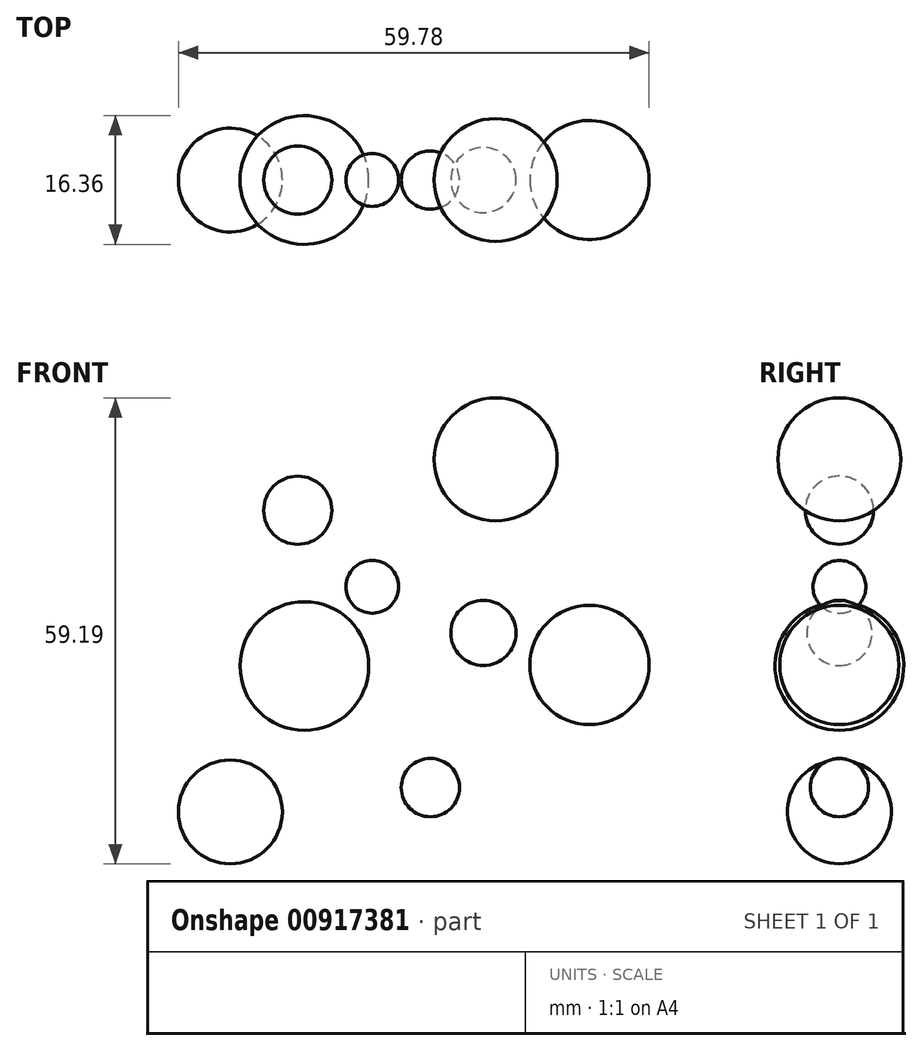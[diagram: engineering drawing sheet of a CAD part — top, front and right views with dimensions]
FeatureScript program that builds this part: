
annotation { "Feature Type Name" : "Feature", "Feature Type Description" : "" }
export const myFeature = defineFeature(function(context is Context, id is Id, definition is map)
    precondition{}
    {
        {
            var Q0;
            Q0=qCreatedBy(makeId("Front.planeOp"),FACE);
            var sketch = newSketch(context, id + "F0", { "sketchPlane" : qUnion([Q0])});
            skCircle(sketch, "E0", {"center": v(0, 0) * mm, "radius": 3.35 * mm});
            skCircle(sketch, "E1", {"center": v(15.65, 16.19) * mm, "radius": 7.81 * mm});
            skCircle(sketch, "E2", {"center": v(-9.47, 9.73) * mm, "radius": 4.34 * mm});
            skCircle(sketch, "E3", {"center": v(-8.63, -10.06) * mm, "radius": 8.18 * mm});
            skCircle(sketch, "E4", {"center": v(27.59, -9.92) * mm, "radius": 7.57 * mm});
            skCircle(sketch, "E5", {"center": v(14.1, -5.85) * mm, "radius": 4.15 * mm});
            skCircle(sketch, "E6", {"center": v(7.37, -25.5) * mm, "radius": 3.7 * mm});
            skCircle(sketch, "E7", {"center": v(-18.03, -28.6) * mm, "radius": 6.6 * mm});
            skPoint(sketch, "E8", {"position": v(-8.63, -1.89) * mm});
            skPoint(sketch, "E9", {"position": v(-8.63, -18.24) * mm});
            skPoint(sketch, "E10", {"position": v(-18.03, -22) * mm});
            skPoint(sketch, "E11", {"position": v(-18.03, -35.19) * mm});
            skPoint(sketch, "E12", {"position": v(7.37, -21.8) * mm});
            skPoint(sketch, "E13", {"position": v(7.37, -29.2) * mm});
            skPoint(sketch, "E14", {"position": v(27.59, -17.49) * mm});
            skPoint(sketch, "E15", {"position": v(27.59, -2.36) * mm});
            skPoint(sketch, "E16", {"position": v(14.1, -10) * mm});
            skPoint(sketch, "E17", {"position": v(14.1, -1.7) * mm});
            skPoint(sketch, "E18", {"position": v(0, 3.35) * mm});
            skPoint(sketch, "E19", {"position": v(0, -3.35) * mm});
            skPoint(sketch, "E20", {"position": v(-9.47, 14.07) * mm});
            skPoint(sketch, "E21", {"position": v(-9.47, 5.4) * mm});
            skPoint(sketch, "E22", {"position": v(15.65, 8.37) * mm});
            skPoint(sketch, "E23", {"position": v(15.65, 24) * mm});
            skLineSegment(sketch, "E24", {"start": v(-9.47, 14.07) * mm, "end": v(-9.47, 5.4) * mm});
            skLineSegment(sketch, "E25", {"start": v(15.65, 24) * mm, "end": v(15.65, 8.37) * mm});
            skLineSegment(sketch, "E26", {"start": v(-8.63, -1.89) * mm, "end": v(-8.63, -18.24) * mm});
            skLineSegment(sketch, "E27", {"start": v(-18.03, -22) * mm, "end": v(-18.03, -35.19) * mm});
            skLineSegment(sketch, "E28", {"start": v(7.37, -21.8) * mm, "end": v(7.37, -29.2) * mm});
            skLineSegment(sketch, "E29", {"start": v(14.1, -1.7) * mm, "end": v(14.1, -10) * mm});
            skLineSegment(sketch, "E30", {"start": v(0, 3.35) * mm, "end": v(0, -3.35) * mm});
            skLineSegment(sketch, "E31", {"start": v(27.59, -17.49) * mm, "end": v(27.59, -2.36) * mm});
            skSolve(sketch);
        }
        {
            var Q0;
            {var subQ0=sQuery(id+"F0.wireOp",EDGE,"E27");Q0=makeQuery(id+"F0.imprint","IMPRINT",FACE,{"disambiguationData":[TD([[makeQuery(id+"F0.imprint","IMPRINT",EDGE,{"derivedFrom":subQ0}),-1.0]])]});}
            var Q1;
            Q1=sQuery(id+"F0.wireOp",EDGE,"E27");
            revolve(context, id + "F1", {"surfaceOperationType" : NewSurfaceOperationType.NEW, "entities" : qUnion([Q0]), "axis" : qUnion([Q1]), "revolveType" : RevolveType.FULL});
        }
        {
            var Q0;
            {var subQ0=sQuery(id+"F0.wireOp",EDGE,"E26");Q0=makeQuery(id+"F0.imprint","IMPRINT",FACE,{"disambiguationData":[TD([[makeQuery(id+"F0.imprint","IMPRINT",EDGE,{"derivedFrom":subQ0}),-1.0]])]});}
            var Q1;
            Q1=sQuery(id+"F0.wireOp",EDGE,"E26");
            revolve(context, id + "F2", {"surfaceOperationType" : NewSurfaceOperationType.NEW, "entities" : qUnion([Q0]), "axis" : qUnion([Q1]), "revolveType" : RevolveType.FULL});
        }
        {
            var Q0;
            {var subQ0=sQuery(id+"F0.wireOp",EDGE,"E24");Q0=makeQuery(id+"F0.imprint","IMPRINT",FACE,{"disambiguationData":[TD([[makeQuery(id+"F0.imprint","IMPRINT",EDGE,{"derivedFrom":subQ0}),-1.0]])]});}
            var Q1;
            Q1=sQuery(id+"F0.wireOp",EDGE,"E24");
            revolve(context, id + "F3", {"surfaceOperationType" : NewSurfaceOperationType.NEW, "entities" : qUnion([Q0]), "axis" : qUnion([Q1]), "revolveType" : RevolveType.FULL});
        }
        {
            var Q0;
            {var subQ0=sQuery(id+"F0.wireOp",EDGE,"E25");Q0=makeQuery(id+"F0.imprint","IMPRINT",FACE,{"disambiguationData":[TD([[makeQuery(id+"F0.imprint","IMPRINT",EDGE,{"derivedFrom":subQ0}),-1.0]])]});}
            var Q1;
            Q1=sQuery(id+"F0.wireOp",EDGE,"E25");
            revolve(context, id + "F4", {"surfaceOperationType" : NewSurfaceOperationType.NEW, "entities" : qUnion([Q0]), "axis" : qUnion([Q1]), "revolveType" : RevolveType.FULL});
        }
        {
            var Q0;
            {var subQ0=sQuery(id+"F0.wireOp",EDGE,"E30");Q0=makeQuery(id+"F0.imprint","IMPRINT",FACE,{"disambiguationData":[TD([[makeQuery(id+"F0.imprint","IMPRINT",EDGE,{"derivedFrom":subQ0}),-1.0]])]});}
            var Q1;
            Q1=sQuery(id+"F0.wireOp",EDGE,"E30");
            revolve(context, id + "F5", {"surfaceOperationType" : NewSurfaceOperationType.NEW, "entities" : qUnion([Q0]), "axis" : qUnion([Q1]), "revolveType" : RevolveType.FULL});
        }
        {
            var Q0;
            {var subQ0=sQuery(id+"F0.wireOp",EDGE,"E29");Q0=makeQuery(id+"F0.imprint","IMPRINT",FACE,{"disambiguationData":[TD([[makeQuery(id+"F0.imprint","IMPRINT",EDGE,{"derivedFrom":subQ0}),-1.0]])]});}
            var Q1;
            Q1=sQuery(id+"F0.wireOp",EDGE,"E29");
            revolve(context, id + "F6", {"surfaceOperationType" : NewSurfaceOperationType.NEW, "entities" : qUnion([Q0]), "axis" : qUnion([Q1]), "revolveType" : RevolveType.FULL});
        }
        {
            var Q0;
            {var subQ0=sQuery(id+"F0.wireOp",EDGE,"E28");Q0=makeQuery(id+"F0.imprint","IMPRINT",FACE,{"disambiguationData":[TD([[makeQuery(id+"F0.imprint","IMPRINT",EDGE,{"derivedFrom":subQ0}),-1.0]])]});}
            var Q1;
            Q1=sQuery(id+"F0.wireOp",EDGE,"E28");
            revolve(context, id + "F7", {"surfaceOperationType" : NewSurfaceOperationType.NEW, "entities" : qUnion([Q0]), "axis" : qUnion([Q1]), "revolveType" : RevolveType.FULL});
        }
        {
            var Q0;
            {var subQ0=sQuery(id+"F0.wireOp",EDGE,"E31");Q0=makeQuery(id+"F0.imprint","IMPRINT",FACE,{"disambiguationData":[TD([[makeQuery(id+"F0.imprint","IMPRINT",EDGE,{"derivedFrom":subQ0}),1.0]])]});}
            var Q1;
            Q1=sQuery(id+"F0.wireOp",EDGE,"E31");
            revolve(context, id + "F8", {"surfaceOperationType" : NewSurfaceOperationType.NEW, "entities" : qUnion([Q0]), "axis" : qUnion([Q1]), "revolveType" : RevolveType.FULL});
        }
    });
